# Revit family: Camera-Security-Panasonic-Super_Dynamic-H265_iA-Network-WV-U2130LSeriesX
name_source: partatom
category: Security Devices
units: mm (PartAtom-declared; Revit-internal decimal feet)

## family parameters
Cut with Voids When Loaded = No
Host = Face
Maintain Annotation Orientation = No
OmniClass Number = 23.85.10.14.11
OmniClass Title = Cameras
Part Type = Normal
Room Calculation Point = No
Round Connector Dimension = Use Diameter
Shared = No

## types (2) — shared parameters
Accessory Part = WV-QDC500S
Communication Ports = 10Base-T / 100Base-TX, RJ45 connector
Date Last Modified = 2020/04/07
Day Or Night = Yes
Diameter = 4.291 "
Equipment Abbreviation = SC
Family Version = 1.0.0
HFOV Max 169 = 100.00°
HFOV Min 169 = 100.00°
Has POE = Yes
Height = 2.441 "
IP Or Analog = IP
Indoor Or Outdoor = Indoor
Manufacturer = Panasonic
Model Disclaimer = Contact Panasonic for more information
Mounting Positions = Surface Mount
Operational Humidity = 10 to 90% (no condensation)
Operational Temperature = -10 °C to +50 °C (+14 °F to +122 °F)
Pan Max = 175.00°
Pan Min = -175.00°
Panning Range = -175 to +175
Product Documentation Link = https://bizpartner.panasonic.net
Product Material = Paint - Panasonic - i-PRO White
Product Page URL = https://security.panasonic.com
Provide Feedback = https://www.surveymonkey.com
Regulatory Compliance = UL (UL60950-1), c-UL (CSA C22.2 No.60950-1), CE, IEC60950-1, FCC (Part15 ClassA), ICES003 ClassA, EN55032 ClassB, EN55024
Storage Temperature = -10 °C to +50 °C (+14 °F to +122 °F)
Tilt Max = 80.00°
Tilt Min = -30.00°
Tilting Range = -30 to +80
URL = http://security.panasonic.com
VFOV Max 169 = 54.00°
VFOV Min 169 = 54.00°
Vandal Resistant = No
Voltage DC = 48 V
Weight = 0.55 lb
Wide Dynamic Range = Yes
Yaw Max = 100.00°
Yaw Min = -100.00°
Yawing Range = -100 to +100
z Base Height = 1.177 "
z Base Radius = 2.146 "
z Bracket Radius = 3.661 "
z Const Pan Handle Length = 19.488 "
z Const Tilt Base Length = 9.843 "
z Const Tilt Base2 Length = 19.685 "
z Const Tilt Handle Length = 11.811 "
z Const Yaw Base Length = 10.236 "
z Const Yaw Base2 Length = 17.323 "
z Const Yaw Handle Length = 9.252 "
z Dome Material = Glass - Panasonic - Smoked
z Dome Radius = 1.264 "
z VV Face Radius = 4.626 "
z VV Origin Height Offset = 0.217 "
z VV Viewpoint Depth Max = 0.849 "
z VV Viewpoint Depth Min = 0.849 "
zero-valued in all types: Default Elevation, z Zero

## per-type parameters (varying)
| type | Angle Of View | Description | HFOV Max 43 | HFOV Min 43 | Minimum Illumination | Part Description | Power Active | VFOV Max 43 | VFOV Min 43 | z Camera Type |
| WV-U2130L | 100 | Security Camera, H.265 iA, Network, Super Dynamic FullHD, WV-U2130L | 81.00° | 81.00° | 0.100 lx | Security Camera, H.265 iA, Network, Super Dynamic FullHD, WV-U2130L | 4.8 W | 60.00° | 60.00° | 1 |
| WV-U2140L | 102 | Security Camera, H.265 Varifocal Fixed Dome, Network, Super Dynamic WQHD, WV-U2142L | 100.00° | 100.00° | 0.300 lx | Security Camera, H.265 Varifocal Fixed Dome, Network, Super Dynamic WQHD, WV-U2142L | 5.3 W | 54.00° | 54.00° | 2 |

note: column(s) folded — value = type name in every type: Model, Part Number

## geometry (parser evidence)
native form markers: Sweep x8
no freeform markers — native parametric forms only
